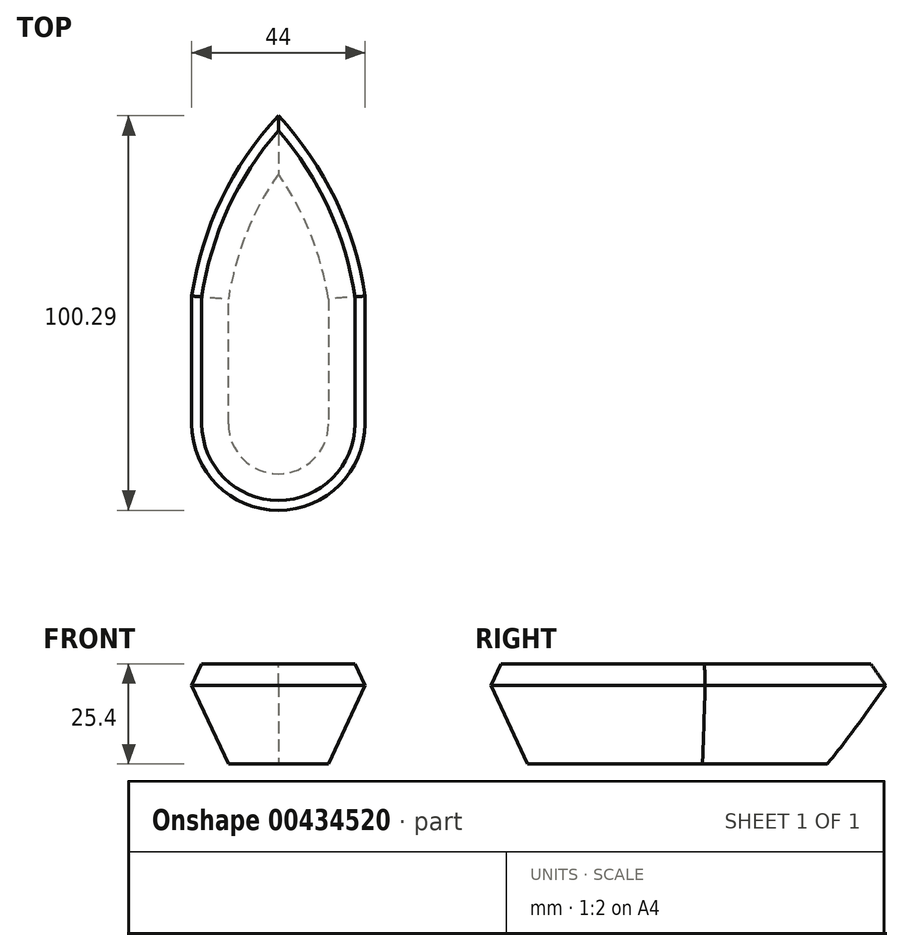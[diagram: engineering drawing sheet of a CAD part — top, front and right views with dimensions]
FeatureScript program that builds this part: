
annotation { "Feature Type Name" : "Feature", "Feature Type Description" : "" }
export const myFeature = defineFeature(function(context is Context, id is Id, definition is map)
    precondition{}
    {
        {
            var Q0;
            Q0=qCreatedBy(makeId("Top.planeOp"),FACE);
            var sketch = newSketch(context, id + "F0", { "sketchPlane" : qUnion([Q0])});
            skLineSegment(sketch, "E0.bottom", {"start": v(12.7, 38.1) * mm, "end": v(-12.7, 38.1) * mm});
            skLineSegment(sketch, "E0.top", {"start": v(12.7, -38.1) * mm, "end": v(-12.7, -38.1) * mm});
            skLineSegment(sketch, "E0.left", {"start": v(12.7, 38.1) * mm, "end": v(12.7, -38.1) * mm});
            skLineSegment(sketch, "E0.right", {"start": v(-12.7, 38.1) * mm, "end": v(-12.7, -38.1) * mm});
            skPoint(sketch, "E0.middle", {"position": v(0, 0) * mm});
            skArc(sketch, "E1", {"start": v(0, 38.1) * mm, "mid": v(-8.15, 22.95) * mm, "end": v(-12.7, 6.35) * mm});
            skArc(sketch, "E2", {"start": v(12.7, 6.35) * mm, "mid": v(8.15, 22.95) * mm, "end": v(0, 38.1) * mm});
            skLineSegment(sketch, "E3", {"start": v(-12.7, 6.35) * mm, "end": v(-12.7, 38.1) * mm});
            skLineSegment(sketch, "E4", {"start": v(12.7, 6.35) * mm, "end": v(12.7, 38.1) * mm});
            skArc(sketch, "E5", {"start": v(-12.7, -25.4) * mm, "mid": v(0, -38.1) * mm, "end": v(12.7, -25.4) * mm});
            skPoint(sketch, "E6", {"position": v(0, -38.1) * mm});
            skSolve(sketch);
        }
        {
            var Q0;
            {var subQ0=sQuery(id+"F0.wireOp",EDGE,"E1");Q0=makeQuery(id+"F0.imprint","IMPRINT",FACE,{"disambiguationData":[TD([[makeQuery(id+"F0.imprint","IMPRINT",EDGE,{"derivedFrom":subQ0}),1.0]])]});}
            extrude(context, id + "F1", {"entities" : qUnion([Q0]), "depth" : 25.4 * mm, "hasDraft" : true, "draftAngle" : 25 * degree});
        }
        {
            var Q0;
            Q0=makeQuery(id+"F1.opExtrude","CAP_FACE",FACE,{"disambiguationData":[OSD([sQuery(id+"F0.wireOp",EDGE,"E0.left"),sQuery(id+"F0.wireOp",EDGE,"E0.right"),sQuery(id+"F0.wireOp",EDGE,"E1"),sQuery(id+"F0.wireOp",EDGE,"E2"),sQuery(id+"F0.wireOp",EDGE,"E5")])],"isStart":false});
            var sketch = newSketch(context, id + "F2", { "sketchPlane" : qUnion([Q0])});
            skArc(sketch, "E7.0", {"start": v(19.46, -25.4) * mm, "mid": v(0, -44.86) * mm, "end": v(-19.46, -25.4) * mm});
            skLineSegment(sketch, "E7.1", {"start": v(19.46, 6.86) * mm, "end": v(19.46, -25.4) * mm});
            skLineSegment(sketch, "E7.2", {"start": v(-19.46, 6.86) * mm, "end": v(-19.46, -25.4) * mm});
            skArc(sketch, "E7.3", {"start": v(-19.46, 6.86) * mm, "mid": v(-12.75, 29.37) * mm, "end": v(0, 49.1) * mm});
            skArc(sketch, "E7.4", {"start": v(0, 49.1) * mm, "mid": v(12.75, 29.37) * mm, "end": v(19.46, 6.86) * mm});
            skLineSegment(sketch, "E8.0", {"start": v(24.54, 7.23) * mm, "end": v(24.54, -25.4) * mm});
            skLineSegment(sketch, "E9", {"start": v(19.46, -0.67) * mm, "end": v(24.54, -0.67) * mm});
            skSolve(sketch);
        }
        {
            var Q0;
            {var subQ1=sQuery(id+"F2.wireOp",EDGE,"E7.0");Q0=makeQuery(id+"F2.imprint","IMPRINT",FACE,{"disambiguationData":[TD([[makeQuery(id+"F2.imprint","IMPRINT",EDGE,{"derivedFrom":subQ1}),-1.0]])]});}
            extrude(context, id + "F3", {"entities" : qUnion([Q0]), "operationType" : NewBodyOperationType.REMOVE, "oppositeDirection" : true, "depth" : 20.32 * mm, "hasDraft" : true, "draftAngle" : 25 * degree, "draftPullDirection" : true});
        }
    });
